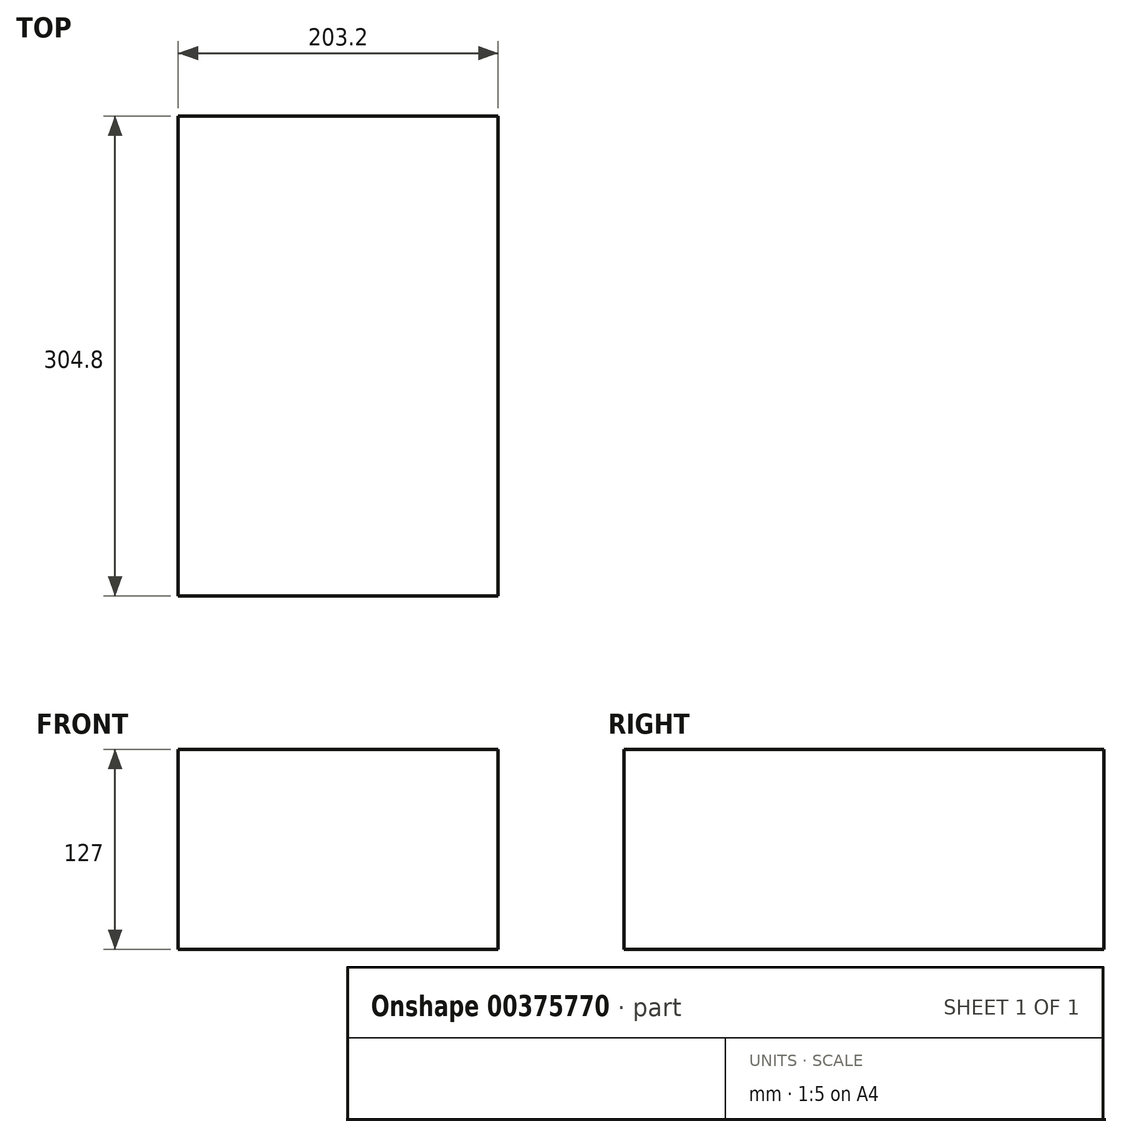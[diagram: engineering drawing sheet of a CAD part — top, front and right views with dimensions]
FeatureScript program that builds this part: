
annotation { "Feature Type Name" : "Feature", "Feature Type Description" : "" }
export const myFeature = defineFeature(function(context is Context, id is Id, definition is map)
    precondition{}
    {
        {
            var Q0;
            Q0=qCreatedBy(makeId("Top.planeOp"),FACE);
            var sketch = newSketch(context, id + "F0", { "sketchPlane" : qUnion([Q0])});
            skLineSegment(sketch, "E0", {"start": v(-101.6, 0) * mm, "end": v(-101.6, 304.8) * mm});
            skLineSegment(sketch, "E1", {"start": v(101.6, 0) * mm, "end": v(101.6, 304.8) * mm});
            skLineSegment(sketch, "E2", {"start": v(101.6, 304.8) * mm, "end": v(-101.6, 304.8) * mm});
            skLineSegment(sketch, "E3", {"start": v(101.6, 0) * mm, "end": v(-101.6, 0) * mm});
            skSolve(sketch);
        }
        {
            var Q0;
            Q0=makeQuery(id+"F0.imprint","IMPRINT",FACE,{"disambiguationData":[TD([[makeQuery(id+"F0.imprint","IMPRINT",EDGE,{"derivedFrom":sQuery(id+"F0.wireOp",EDGE,"E0")}),-1.0]])]});
            extrude(context, id + "F1", {"entities" : qUnion([Q0]), "depth" : 127 * mm});
        }
    });
